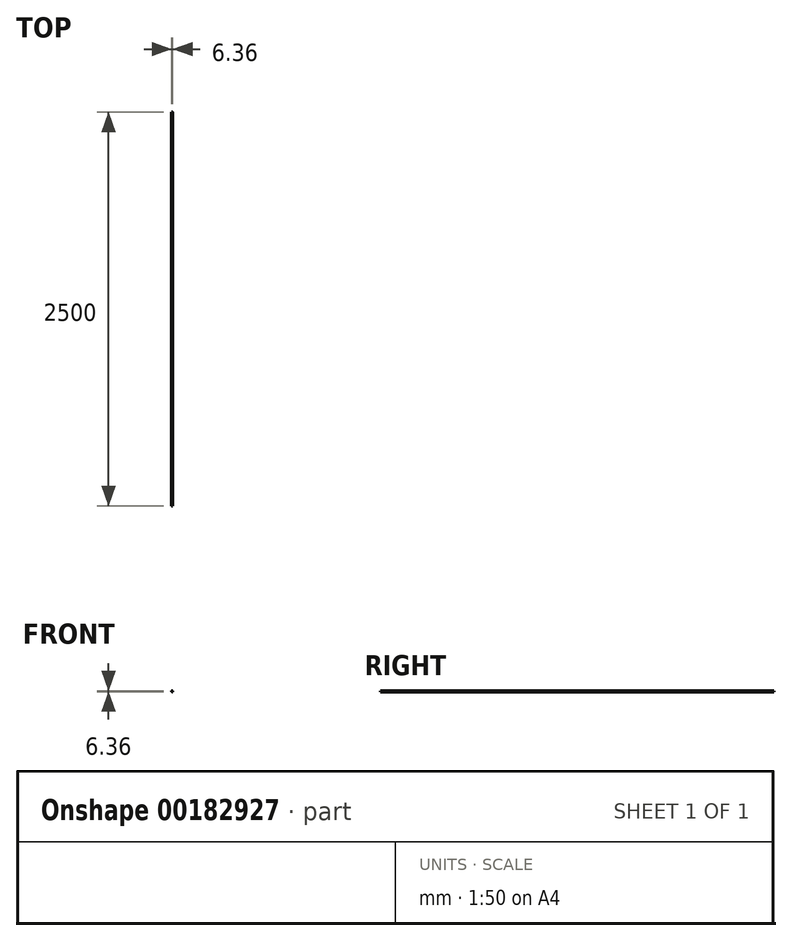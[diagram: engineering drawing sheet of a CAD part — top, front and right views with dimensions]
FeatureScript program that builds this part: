
annotation { "Feature Type Name" : "Feature", "Feature Type Description" : "" }
export const myFeature = defineFeature(function(context is Context, id is Id, definition is map)
    precondition{}
    {
        {
            var Q0;
            Q0=qCreatedBy(makeId("Front.planeOp"),FACE);
            var sketch = newSketch(context, id + "F0", { "sketchPlane" : qUnion([Q0])});
            skCircle(sketch, "E0", {"center": v(0, 0) * mm, "radius": 3.18 * mm});
            skSolve(sketch);
        }
        {
            var Q0;
            Q0 = qSketchRegion(id + "F0", true);
            extrude(context, id + "F1", {"entities" : qUnion([Q0]), "endBound" : BoundingType.SYMMETRIC, "depth" : 2500 * mm});
        }
    });
